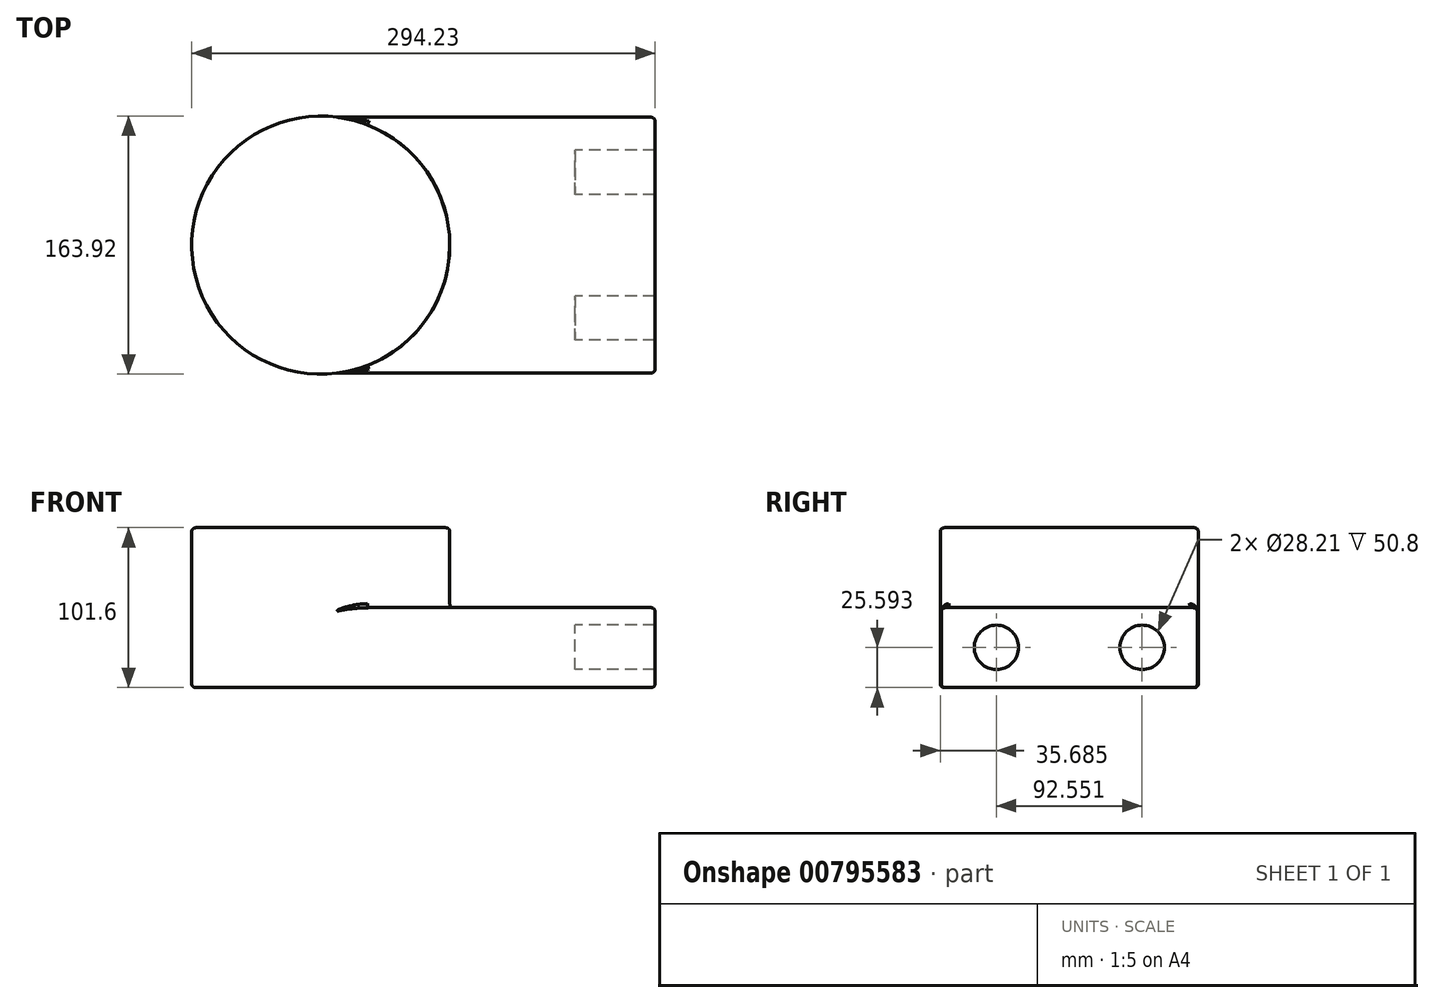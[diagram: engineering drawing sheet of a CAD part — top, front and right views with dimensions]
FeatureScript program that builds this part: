
annotation { "Feature Type Name" : "Feature", "Feature Type Description" : "" }
export const myFeature = defineFeature(function(context is Context, id is Id, definition is map)
    precondition{}
    {
        {
            var Q0;
            Q0=qCreatedBy(makeId("Top.planeOp"),FACE);
            var sketch = newSketch(context, id + "F0", { "sketchPlane" : qUnion([Q0])});
            skLineSegment(sketch, "E0.bottom", {"start": v(80.74, -81.3) * mm, "end": v(-80.74, -81.3) * mm});
            skLineSegment(sketch, "E0.top", {"start": v(80.74, 81.3) * mm, "end": v(-80.74, 81.3) * mm});
            skLineSegment(sketch, "E0.left", {"start": v(80.74, -81.3) * mm, "end": v(80.74, 81.3) * mm});
            skLineSegment(sketch, "E0.right", {"start": v(-80.74, -81.3) * mm, "end": v(-80.74, 81.3) * mm});
            skPoint(sketch, "E0.middle", {"position": v(0, 0) * mm});
            skCircle(sketch, "E1", {"center": v(-80.74, 0) * mm, "radius": 81.96 * mm});
            skSolve(sketch);
        }
        {
            var Q0;
            {var subQ0=sQuery(id+"F0.wireOp",EDGE,"E0.right");Q0=makeQuery(id+"F0.imprint","IMPRINT",FACE,{"disambiguationData":[TD([[makeQuery(id+"F0.imprint","IMPRINT",EDGE,{"derivedFrom":subQ0}),1.0]])]});}
            var Q1;
            {var subQ0=sQuery(id+"F0.wireOp",EDGE,"E0.right");Q1=makeQuery(id+"F0.imprint","IMPRINT",FACE,{"disambiguationData":[TD([[makeQuery(id+"F0.imprint","IMPRINT",EDGE,{"derivedFrom":subQ0}),-1.0]])]});}
            extrude(context, id + "F1", {"entities" : qUnion([Q0, Q1]), "depth" : 101.6 * mm, "offsetDistance" : 25.4 * mm});
        }
        {
            var Q0;
            {var subQ0=sQuery(id+"F0.wireOp",EDGE,"E0.left");Q0=makeQuery(id+"F0.imprint","IMPRINT",FACE,{"disambiguationData":[TD([[makeQuery(id+"F0.imprint","IMPRINT",EDGE,{"derivedFrom":subQ0}),1.0]])]});}
            extrude(context, id + "F2", {"entities" : qUnion([Q0]), "operationType" : NewBodyOperationType.ADD, "depth" : 50.8 * mm, "offsetDistance" : 25.4 * mm});
        }
        {
            var Q0;
            Q0=makeQuery(id+"F2.opExtrude","SWEPT_FACE",FACE,{"disambiguationData":[OSD([sQuery(id+"F0.wireOp",EDGE,"E0.left")])]});
            var sketch = newSketch(context, id + "F3", { "sketchPlane" : qUnion([Q0])});
            skCircle(sketch, "E2", {"center": v(-46.28, 25.6) * mm, "radius": 14.1 * mm});
            skLineSegment(sketch, "E3", {"start": v(0, 0) * mm, "end": v(0, 50.8) * mm});
            skCircle(sketch, "E4.MirrorC", {"center": v(46.28, 25.6) * mm, "radius": 14.1 * mm});
            skSolve(sketch);
        }
        {
            var Q0;
            Q0=makeQuery(id+"F3.imprint","IMPRINT",FACE,{"disambiguationData":[TD([[makeQuery(id+"F3.imprint","IMPRINT",EDGE,{"derivedFrom":sQuery(id+"F3.wireOp",EDGE,"E2")}),-1.0]])]});
            var Q1;
            {var subQ3=sQuery(id+"F3.wireOp",EDGE,"E3");Q1=makeQuery(id+"F3.imprint","IMPRINT",FACE,{"disambiguationData":[TD([[makeQuery(id+"F3.imprint","IMPRINT",EDGE,{"derivedFrom":subQ3}),-1.0]])]});}
            extrude(context, id + "F4", {"entities" : qUnion([Q0, Q1]), "operationType" : NewBodyOperationType.ADD, "depth" : 50.8 * mm, "offsetDistance" : 25.4 * mm});
        }
        {
            var Q0;
            Q0=makeQuery(id+"F1.opExtrude","CAP_EDGE",EDGE,{"disambiguationData":[OSD([sQuery(id+"F0.wireOp",EDGE,"E1")])],"isStart":false});
            var Q1;
            Q1=makeQuery(id+"F2.opExtrude","CAP_EDGE",EDGE,{"disambiguationData":[OSD([sQuery(id+"F0.wireOp",EDGE,"E1")])],"isStart":false});
            var Q2;
            {var subQ0=sQuery(id+"F0.wireOp",EDGE,"E0.left");var subQ1=sQuery(id+"F0.wireOp",EDGE,"E0.bottom");Q2=makeQuery(id+"F4.boolean.opBoolean","MERGE",EDGE,{"derivedFrom":[makeQuery(id+"F2.opExtrude","CAP_EDGE",EDGE,{"disambiguationData":[OSD([subQ1])],"isStart":false}),makeQuery(id+"F4.opExtrude","SWEPT_EDGE",EDGE,{"disambiguationData":[OSD([subQ1,subQ0]),TDD([makeQuery(id+"F3.imprint","INTERSECT",VERTEX,{"derivedFrom":[makeQuery(id+"F2.opExtrude","SWEPT_EDGE",EDGE,{"disambiguationData":[OSD([subQ1,subQ0])]}),makeQuery(id+"F2.opExtrude","CAP_EDGE",EDGE,{"disambiguationData":[OSD([subQ0])],"isStart":false})]})])]})]});}
            var Q3;
            {var subQ0=sQuery(id+"F0.wireOp",EDGE,"E0.left");var subQ1=sQuery(id+"F0.wireOp",EDGE,"E0.bottom");Q3=makeQuery(id+"F4.boolean.opBoolean","MERGE",EDGE,{"derivedFrom":[makeQuery(id+"F2.opExtrude","CAP_EDGE",EDGE,{"disambiguationData":[OSD([subQ1])],"isStart":true}),makeQuery(id+"F4.opExtrude","SWEPT_EDGE",EDGE,{"disambiguationData":[OSD([subQ1,subQ0]),TDD([makeQuery(id+"F3.imprint","INTERSECT",VERTEX,{"derivedFrom":[makeQuery(id+"F2.opExtrude","SWEPT_EDGE",EDGE,{"disambiguationData":[OSD([subQ1,subQ0])]}),makeQuery(id+"F2.opExtrude","CAP_EDGE",EDGE,{"disambiguationData":[OSD([subQ0])],"isStart":true})]})])]})]});}
            var Q4;
            Q4=makeQuery(id+"F4.opExtrude","CAP_EDGE",EDGE,{"disambiguationData":[OSD([sQuery(id+"F0.wireOp",EDGE,"E0.bottom"),sQuery(id+"F0.wireOp",EDGE,"E0.left")])],"isStart":false});
            var Q5;
            {var subQ0=sQuery(id+"F0.wireOp",EDGE,"E0.left");var subQ1=makeQuery(id+"F2.opExtrude","CAP_EDGE",EDGE,{"disambiguationData":[OSD([subQ0])],"isStart":false});var subQ2=makeQuery(id+"F3.imprint","INTERSECT",VERTEX,{"derivedFrom":[subQ1,sQuery(id+"F3.wireOp",EDGE,"E3")]});Q5=makeQuery(id+"F4.opExtrude","CAP_EDGE",EDGE,{"disambiguationData":[OSD([subQ0]),TDD([makeQuery(id+"F3.imprint","IMPRINT",EDGE,{"disambiguationData":[TD([[subQ2,1.0]])],"derivedFrom":subQ1}),makeQuery(id+"F3.imprint","IMPRINT",EDGE,{"disambiguationData":[TD([[subQ2,-1.0]])],"derivedFrom":subQ1})])],"isStart":false});}
            var Q6;
            {var subQ0=sQuery(id+"F0.wireOp",EDGE,"E0.left");var subQ1=makeQuery(id+"F2.opExtrude","CAP_EDGE",EDGE,{"disambiguationData":[OSD([subQ0])],"isStart":true});var subQ2=makeQuery(id+"F3.imprint","INTERSECT",VERTEX,{"derivedFrom":[subQ1,sQuery(id+"F3.wireOp",EDGE,"E3")]});Q6=makeQuery(id+"F4.opExtrude","CAP_EDGE",EDGE,{"disambiguationData":[OSD([subQ0]),TDD([makeQuery(id+"F3.imprint","IMPRINT",EDGE,{"disambiguationData":[TD([[subQ2,1.0]])],"derivedFrom":subQ1}),makeQuery(id+"F3.imprint","IMPRINT",EDGE,{"disambiguationData":[TD([[subQ2,-1.0]])],"derivedFrom":subQ1})])],"isStart":false});}
            var Q7;
            Q7=makeQuery(id+"F4.opExtrude","CAP_EDGE",EDGE,{"disambiguationData":[OSD([sQuery(id+"F0.wireOp",EDGE,"E0.top"),sQuery(id+"F0.wireOp",EDGE,"E0.left")])],"isStart":false});
            var Q8;
            {var subQ0=sQuery(id+"F0.wireOp",EDGE,"E0.left");var subQ1=sQuery(id+"F0.wireOp",EDGE,"E0.top");Q8=makeQuery(id+"F4.boolean.opBoolean","MERGE",EDGE,{"derivedFrom":[makeQuery(id+"F2.opExtrude","CAP_EDGE",EDGE,{"disambiguationData":[OSD([subQ1])],"isStart":false}),makeQuery(id+"F4.opExtrude","SWEPT_EDGE",EDGE,{"disambiguationData":[OSD([subQ1,subQ0]),TDD([makeQuery(id+"F3.imprint","INTERSECT",VERTEX,{"derivedFrom":[makeQuery(id+"F2.opExtrude","SWEPT_EDGE",EDGE,{"disambiguationData":[OSD([subQ1,subQ0])]}),makeQuery(id+"F2.opExtrude","CAP_EDGE",EDGE,{"disambiguationData":[OSD([subQ0])],"isStart":false})]})])]})]});}
            var Q9;
            {var subQ0=sQuery(id+"F0.wireOp",EDGE,"E0.left");var subQ1=sQuery(id+"F0.wireOp",EDGE,"E0.top");Q9=makeQuery(id+"F4.boolean.opBoolean","MERGE",EDGE,{"derivedFrom":[makeQuery(id+"F2.opExtrude","CAP_EDGE",EDGE,{"disambiguationData":[OSD([subQ1])],"isStart":true}),makeQuery(id+"F4.opExtrude","SWEPT_EDGE",EDGE,{"disambiguationData":[OSD([subQ1,subQ0]),TDD([makeQuery(id+"F3.imprint","INTERSECT",VERTEX,{"derivedFrom":[makeQuery(id+"F2.opExtrude","SWEPT_EDGE",EDGE,{"disambiguationData":[OSD([subQ1,subQ0])]}),makeQuery(id+"F2.opExtrude","CAP_EDGE",EDGE,{"disambiguationData":[OSD([subQ0])],"isStart":true})]})])]})]});}
            var Q10;
            Q10=makeQuery(id+"F2.opExtrude","SWEPT_EDGE",EDGE,{"disambiguationData":[OSD([sQuery(id+"F0.wireOp",EDGE,"E0.top"),sQuery(id+"F0.wireOp",EDGE,"E1")])]});
            var Q11;
            Q11=makeQuery(id+"F1.opExtrude","SWEPT_FACE",FACE,{"disambiguationData":[OSD([sQuery(id+"F0.wireOp",EDGE,"E1")])]});
            fillet(context, id + "F5", {"entities" : qUnion([Q0, Q1, Q2, Q3, Q4, Q5, Q6, Q7, Q8, Q9, Q10, Q11]), "radius" : 2.54 * mm, "tangentPropagation" : true, "allowEdgeOverflow" : false});
        }
    });
